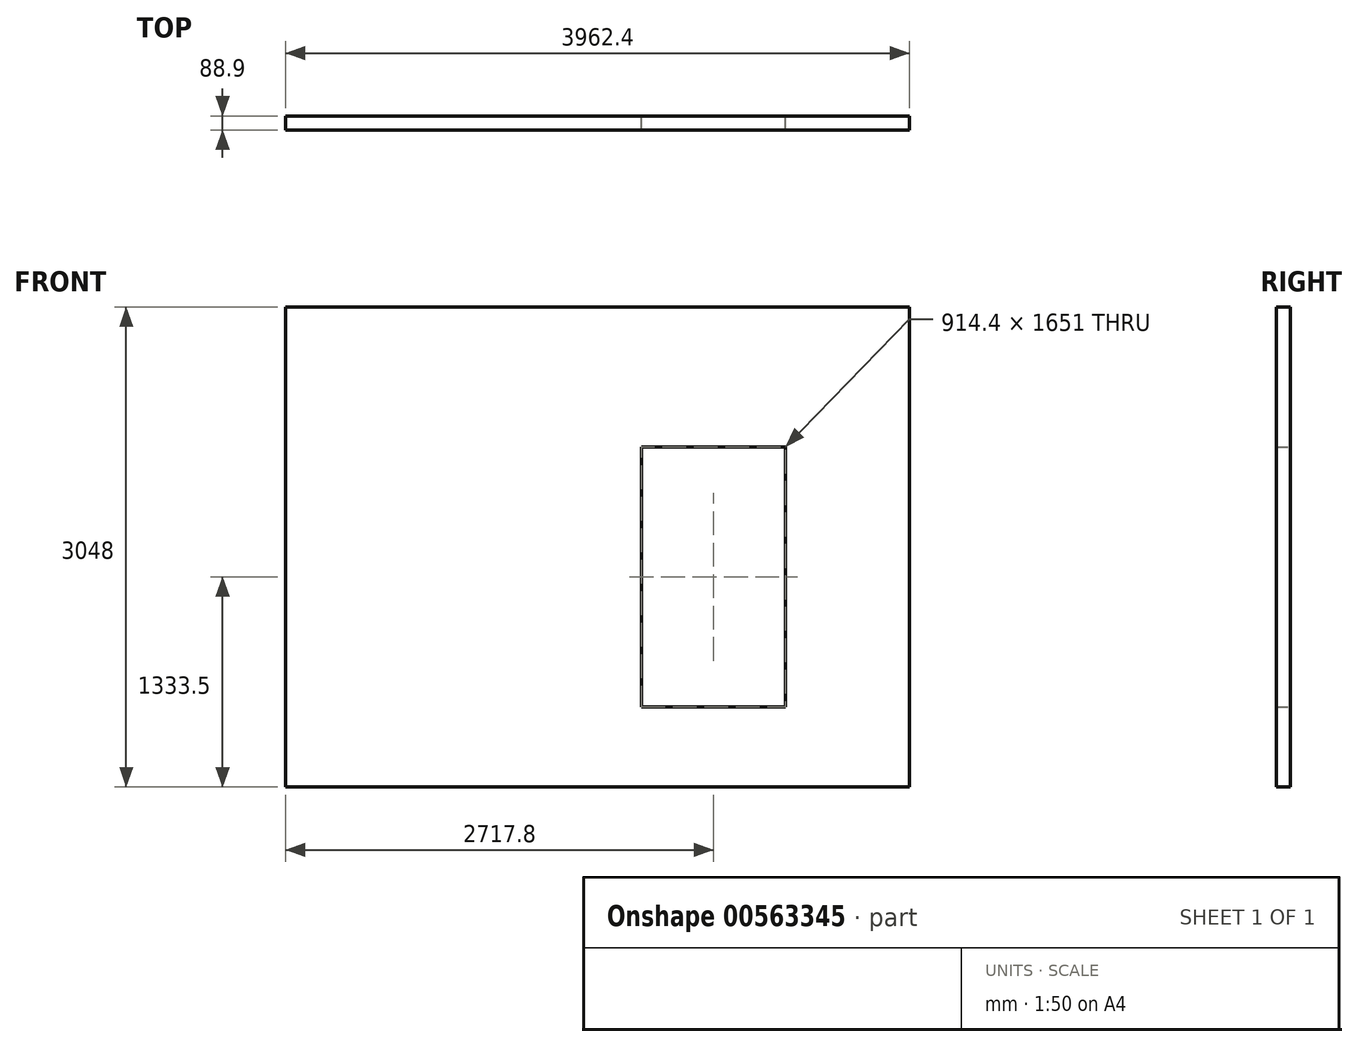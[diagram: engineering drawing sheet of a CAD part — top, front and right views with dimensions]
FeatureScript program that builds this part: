
annotation { "Feature Type Name" : "Feature", "Feature Type Description" : "" }
export const myFeature = defineFeature(function(context is Context, id is Id, definition is map)
    precondition{}
    {
        {
            var Q0;
            Q0=qCreatedBy(makeId("Front.planeOp"),FACE);
            var sketch = newSketch(context, id + "F0", { "sketchPlane" : qUnion([Q0])});
            skLineSegment(sketch, "E0.bottom", {"start": v(-1981.2, -1524) * mm, "end": v(1981.2, -1524) * mm});
            skLineSegment(sketch, "E0.top", {"start": v(-1981.2, 1524) * mm, "end": v(1981.2, 1524) * mm});
            skLineSegment(sketch, "E0.left", {"start": v(-1981.2, -1524) * mm, "end": v(-1981.2, 1524) * mm});
            skLineSegment(sketch, "E0.right", {"start": v(1981.2, -1524) * mm, "end": v(1981.2, 1524) * mm});
            skPoint(sketch, "E0.middle", {"position": v(0, 0) * mm});
            skLineSegment(sketch, "E1", {"start": v(279.4, 635) * mm, "end": v(1193.8, 635) * mm});
            skLineSegment(sketch, "E2", {"start": v(1193.8, 635) * mm, "end": v(1193.8, -1016) * mm});
            skLineSegment(sketch, "E3", {"start": v(1193.8, -1016) * mm, "end": v(279.4, -1016) * mm});
            skLineSegment(sketch, "E4", {"start": v(279.4, -1016) * mm, "end": v(279.4, 635) * mm});
            skSolve(sketch);
        }
        {
            var Q0;
            Q0 = qSketchRegion(id + "F0", true);
            extrude(context, id + "F1", {"entities" : qUnion([Q0]), "depth" : 88.9 * mm, "offsetDistance" : 25.4 * mm});
        }
    });
